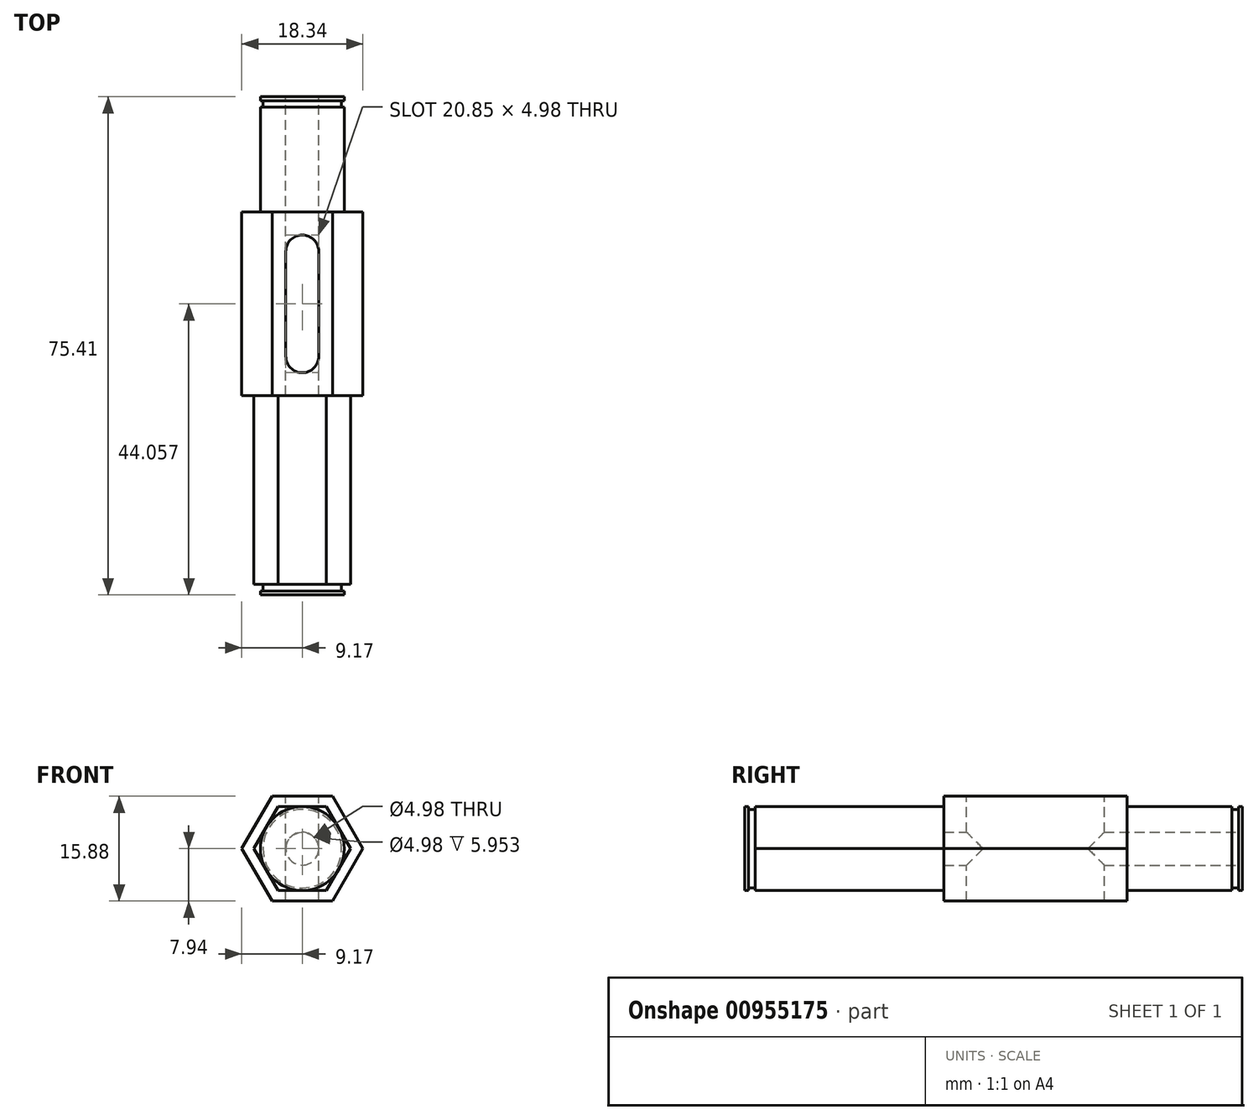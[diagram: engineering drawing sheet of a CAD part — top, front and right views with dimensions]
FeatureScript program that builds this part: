
annotation { "Feature Type Name" : "Feature", "Feature Type Description" : "" }
export const myFeature = defineFeature(function(context is Context, id is Id, definition is map)
    precondition{}
    {
        {
            var Q0;
            Q0=qCreatedBy(makeId("Front.planeOp"),FACE);
            var sketch = newSketch(context, id + "F0", { "sketchPlane" : qUnion([Q0])});
            skCircle(sketch, "E0", {"center": v(0, 0) * mm, "radius": 6.35 * mm});
            skCircle(sketch, "E1", {"center": v(0, 0) * mm, "radius": 2.49 * mm});
            skSolve(sketch);
        }
        {
            var Q0;
            Q0=qSketchRegion(id+"F0",true);
            extrude(context, id + "F1", {"entities" : qUnion([Q0]), "depth" : 17.46 * mm, "offsetDistance" : 25.4 * mm});
        }
        {
            var Q0;
            Q0=makeQuery(id+"F1.opExtrude","CAP_FACE",FACE,{"disambiguationData":[OSD([sQuery(id+"F0.wireOp",EDGE,"E0"),sQuery(id+"F0.wireOp",EDGE,"E1")])],"isStart":false});
            var sketch = newSketch(context, id + "F2", { "sketchPlane" : qUnion([Q0])});
            skCircle(sketch, "E2.cCircle", {"center": v(0, 0) * mm, "radius": 7.94 * mm, "construction": true});
            skLineSegment(sketch, "E2.0", {"start": v(-4.58, 7.94) * mm, "end": v(4.58, 7.94) * mm});
            skLineSegment(sketch, "E2.1", {"start": v(4.58, 7.94) * mm, "end": v(9.17, 0) * mm});
            skLineSegment(sketch, "E2.2", {"start": v(9.17, 0) * mm, "end": v(4.58, -7.94) * mm});
            skLineSegment(sketch, "E2.3", {"start": v(4.58, -7.94) * mm, "end": v(-4.58, -7.94) * mm});
            skLineSegment(sketch, "E2.4", {"start": v(-4.58, -7.94) * mm, "end": v(-9.17, 0) * mm});
            skLineSegment(sketch, "E2.5", {"start": v(-9.17, 0) * mm, "end": v(-4.58, 7.94) * mm});
            skPoint(sketch, "E2.0.midPoint", {"position": v(0, 7.94) * mm});
            skCircle(sketch, "E3", {"center": v(0, 0) * mm, "radius": 2.49 * mm});
            skSolve(sketch);
        }
        {
            var Q0;
            Q0=qSketchRegion(id+"F2",true);
            extrude(context, id + "F3", {"entities" : qUnion([Q0]), "operationType" : NewBodyOperationType.ADD, "depth" : 27.78 * mm, "offsetDistance" : 25.4 * mm});
        }
        {
            var Q0;
            Q0=makeQuery(id+"F3.opExtrude","SWEPT_FACE",FACE,{"disambiguationData":[OSD([sQuery(id+"F2.wireOp",EDGE,"E2.0")])]});
            var sketch = newSketch(context, id + "F4", { "sketchPlane" : qUnion([Q0])});
            skLineSegment(sketch, "E4", {"start": v(0, -23.42) * mm, "end": v(0, -39.3) * mm, "construction": true});
            skArc(sketch, "E5.0.startCap", {"start": v(-2.49, -23.42) * mm, "mid": v(0, -20.93) * mm, "end": v(2.49, -23.42) * mm});
            skArc(sketch, "E5.0.endCap", {"start": v(2.49, -39.3) * mm, "mid": v(0, -41.78) * mm, "end": v(-2.49, -39.3) * mm});
            skLineSegment(sketch, "E5.0.left", {"start": v(2.49, -23.42) * mm, "end": v(2.49, -39.3) * mm});
            skLineSegment(sketch, "E5.0.right", {"start": v(-2.49, -23.42) * mm, "end": v(-2.49, -39.3) * mm});
            skPoint(sketch, "E6", {"position": v(0, -17.46) * mm});
            skLineSegment(sketch, "E7", {"start": v(0, -31.35) * mm, "end": v(4.58, -31.35) * mm, "construction": true});
            skSolve(sketch);
        }
        {
            var Q0;
            Q0=qSketchRegion(id+"F4",true);
            extrude(context, id + "F5", {"entities" : qUnion([Q0]), "operationType" : NewBodyOperationType.REMOVE, "endBound" : BoundingType.THROUGH_ALL, "oppositeDirection" : true, "depth" : 25.4 * mm, "offsetDistance" : 25.4 * mm});
        }
        {
            var Q0;
            Q0=makeQuery(id+"F3.opExtrude","CAP_FACE",FACE,{"disambiguationData":[OSD([sQuery(id+"F2.wireOp",EDGE,"E2.0"),sQuery(id+"F2.wireOp",EDGE,"E2.1"),sQuery(id+"F2.wireOp",EDGE,"E2.2"),sQuery(id+"F2.wireOp",EDGE,"E2.3"),sQuery(id+"F2.wireOp",EDGE,"E2.4"),sQuery(id+"F2.wireOp",EDGE,"E2.5"),sQuery(id+"F2.wireOp",EDGE,"E3")])],"isStart":false});
            var sketch = newSketch(context, id + "F6", { "sketchPlane" : qUnion([Q0])});
            skCircle(sketch, "E8.cCircle", {"center": v(0, 0) * mm, "radius": 6.35 * mm, "construction": true});
            skLineSegment(sketch, "E8.0", {"start": v(3.67, -6.35) * mm, "end": v(-3.67, -6.35) * mm});
            skLineSegment(sketch, "E8.1", {"start": v(-3.67, -6.35) * mm, "end": v(-7.33, 0) * mm});
            skLineSegment(sketch, "E8.2", {"start": v(-7.33, 0) * mm, "end": v(-3.67, 6.35) * mm});
            skLineSegment(sketch, "E8.3", {"start": v(-3.67, 6.35) * mm, "end": v(3.67, 6.35) * mm});
            skLineSegment(sketch, "E8.4", {"start": v(3.67, 6.35) * mm, "end": v(7.33, 0) * mm});
            skLineSegment(sketch, "E8.5", {"start": v(7.33, 0) * mm, "end": v(3.67, -6.35) * mm});
            skPoint(sketch, "E8.0.midPoint", {"position": v(0, -6.35) * mm});
            skSolve(sketch);
        }
        {
            var Q0;
            Q0=qSketchRegion(id+"F6",true);
            extrude(context, id + "F7", {"entities" : qUnion([Q0]), "operationType" : NewBodyOperationType.ADD, "depth" : 30.16 * mm, "offsetDistance" : 25.4 * mm});
        }
        {
            var Q0;
            Q0=qCreatedBy(makeId("Top.planeOp"),FACE);
            var sketch = newSketch(context, id + "F8", { "sketchPlane" : qUnion([Q0])});
            skLineSegment(sketch, "E9", {"start": v(-6.35, -75.4) * mm, "end": v(-6.35, -74.8) * mm});
            skLineSegment(sketch, "E10", {"start": v(-6.35, -74.8) * mm, "end": v(-5.94, -74.8) * mm});
            skLineSegment(sketch, "E11", {"start": v(-5.94, -74.8) * mm, "end": v(-5.94, -73.82) * mm});
            skLineSegment(sketch, "E12", {"start": v(-5.94, -73.82) * mm, "end": v(-7.33, -73.82) * mm});
            skLineSegment(sketch, "E13", {"start": v(0, -75.4) * mm, "end": v(0, -45.24) * mm, "construction": true});
            skLineSegment(sketch, "E14.MirrorCS", {"start": v(6.35, -75.4) * mm, "end": v(6.35, -74.8) * mm});
            skLineSegment(sketch, "E15.MirrorCS", {"start": v(5.94, -73.82) * mm, "end": v(7.33, -73.82) * mm});
            skLineSegment(sketch, "E16.MirrorCS", {"start": v(5.94, -74.8) * mm, "end": v(5.94, -73.82) * mm});
            skLineSegment(sketch, "E17.MirrorCS", {"start": v(6.35, -74.8) * mm, "end": v(5.94, -74.8) * mm});
            skLineSegment(sketch, "E18", {"start": v(0, -75.4) * mm, "end": v(0, 0) * mm, "construction": true});
            skLineSegment(sketch, "E19", {"start": v(0, -37.7) * mm, "end": v(-9.17, -37.7) * mm, "construction": true});
            skLineSegment(sketch, "E20", {"start": v(-7.33, -73.82) * mm, "end": v(-7.33, -75.4) * mm});
            skLineSegment(sketch, "E21", {"start": v(-7.33, -75.4) * mm, "end": v(-6.35, -75.4) * mm});
            skLineSegment(sketch, "E22", {"start": v(7.33, -73.82) * mm, "end": v(7.33, -75.4) * mm});
            skLineSegment(sketch, "E23", {"start": v(7.33, -75.4) * mm, "end": v(6.35, -75.4) * mm});
            skLineSegment(sketch, "E24.MirrorCS", {"start": v(7.33, 0) * mm, "end": v(6.35, 0) * mm});
            skLineSegment(sketch, "E25.MirrorCS", {"start": v(-6.35, -0.6) * mm, "end": v(-5.94, -0.6) * mm});
            skLineSegment(sketch, "E26.MirrorCS", {"start": v(-5.94, -0.6) * mm, "end": v(-5.94, -1.59) * mm});
            skLineSegment(sketch, "E27.MirrorCS", {"start": v(-7.33, 0) * mm, "end": v(-6.35, 0) * mm});
            skLineSegment(sketch, "E28.MirrorCS", {"start": v(5.94, -0.6) * mm, "end": v(5.94, -1.59) * mm});
            skLineSegment(sketch, "E29.MirrorCS", {"start": v(6.35, -0.6) * mm, "end": v(5.94, -0.6) * mm});
            skLineSegment(sketch, "E30.MirrorCS", {"start": v(-5.94, -1.59) * mm, "end": v(-7.33, -1.59) * mm});
            skLineSegment(sketch, "E31.MirrorCS", {"start": v(6.35, 0) * mm, "end": v(6.35, -0.6) * mm});
            skLineSegment(sketch, "E32.MirrorCS", {"start": v(5.94, -1.59) * mm, "end": v(7.33, -1.59) * mm});
            skLineSegment(sketch, "E33.MirrorCS", {"start": v(-6.35, 0) * mm, "end": v(-6.35, -0.6) * mm});
            skLineSegment(sketch, "E34.MirrorCS", {"start": v(-7.33, -1.59) * mm, "end": v(-7.33, 0) * mm});
            skLineSegment(sketch, "E35.MirrorCS", {"start": v(7.33, -1.59) * mm, "end": v(7.33, 0) * mm});
            skSolve(sketch);
        }
        {
            var Q0;
            Q0=qSketchRegion(id+"F8",true);
            var Q1;
            Q1=sQuery(id+"F8.wireOp",EDGE,"E18");
            revolve(context, id + "F9", {"operationType" : NewBodyOperationType.REMOVE, "surfaceOperationType" : NewSurfaceOperationType.NEW, "entities" : qUnion([Q0]), "axis" : qUnion([Q1]), "revolveType" : RevolveType.FULL, "oppositeDirection" : true});
        }
    });
